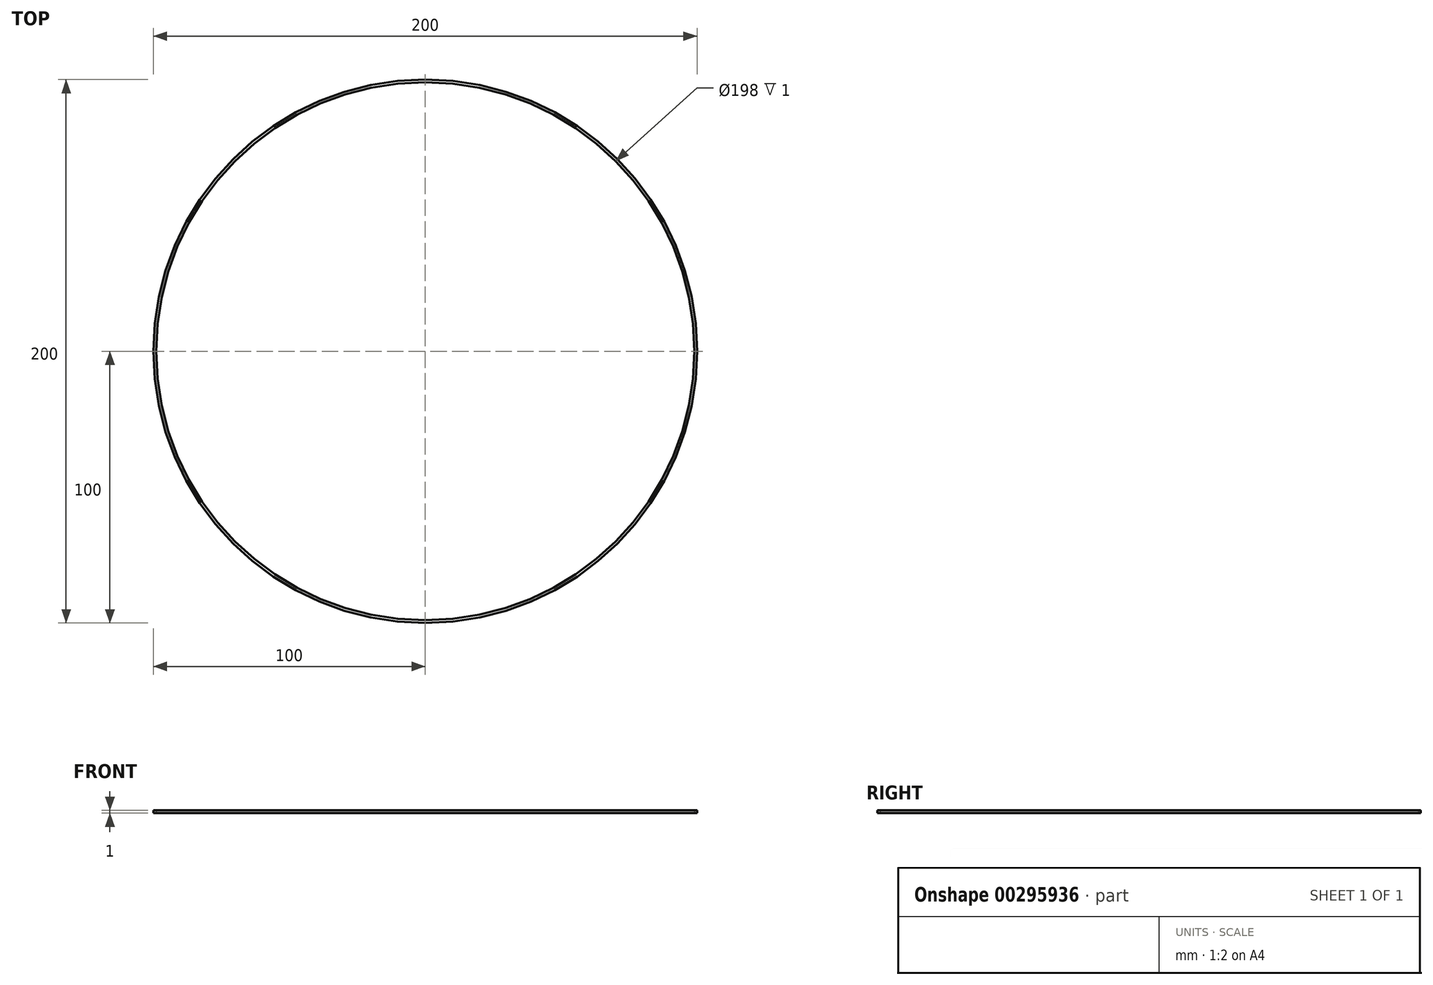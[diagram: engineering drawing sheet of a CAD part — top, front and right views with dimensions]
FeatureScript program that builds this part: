
annotation { "Feature Type Name" : "Feature", "Feature Type Description" : "" }
export const myFeature = defineFeature(function(context is Context, id is Id, definition is map)
    precondition{}
    {
        {
            var Q0;
            Q0=qCreatedBy(makeId("Top.planeOp"),FACE);
            var sketch = newSketch(context, id + "F0", { "sketchPlane" : qUnion([Q0])});
            skCircle(sketch, "E0", {"center": v(0, 0) * mm, "radius": 100 * mm});
            skCircle(sketch, "E1", {"center": v(0, 0) * mm, "radius": 99 * mm});
            skSolve(sketch);
        }
        {
            var Q0;
            Q0 = qSketchRegion(id + "F0", true);
            extrude(context, id + "F1", {"entities" : qUnion([Q0]), "depth" : 1 * mm});
        }
    });
